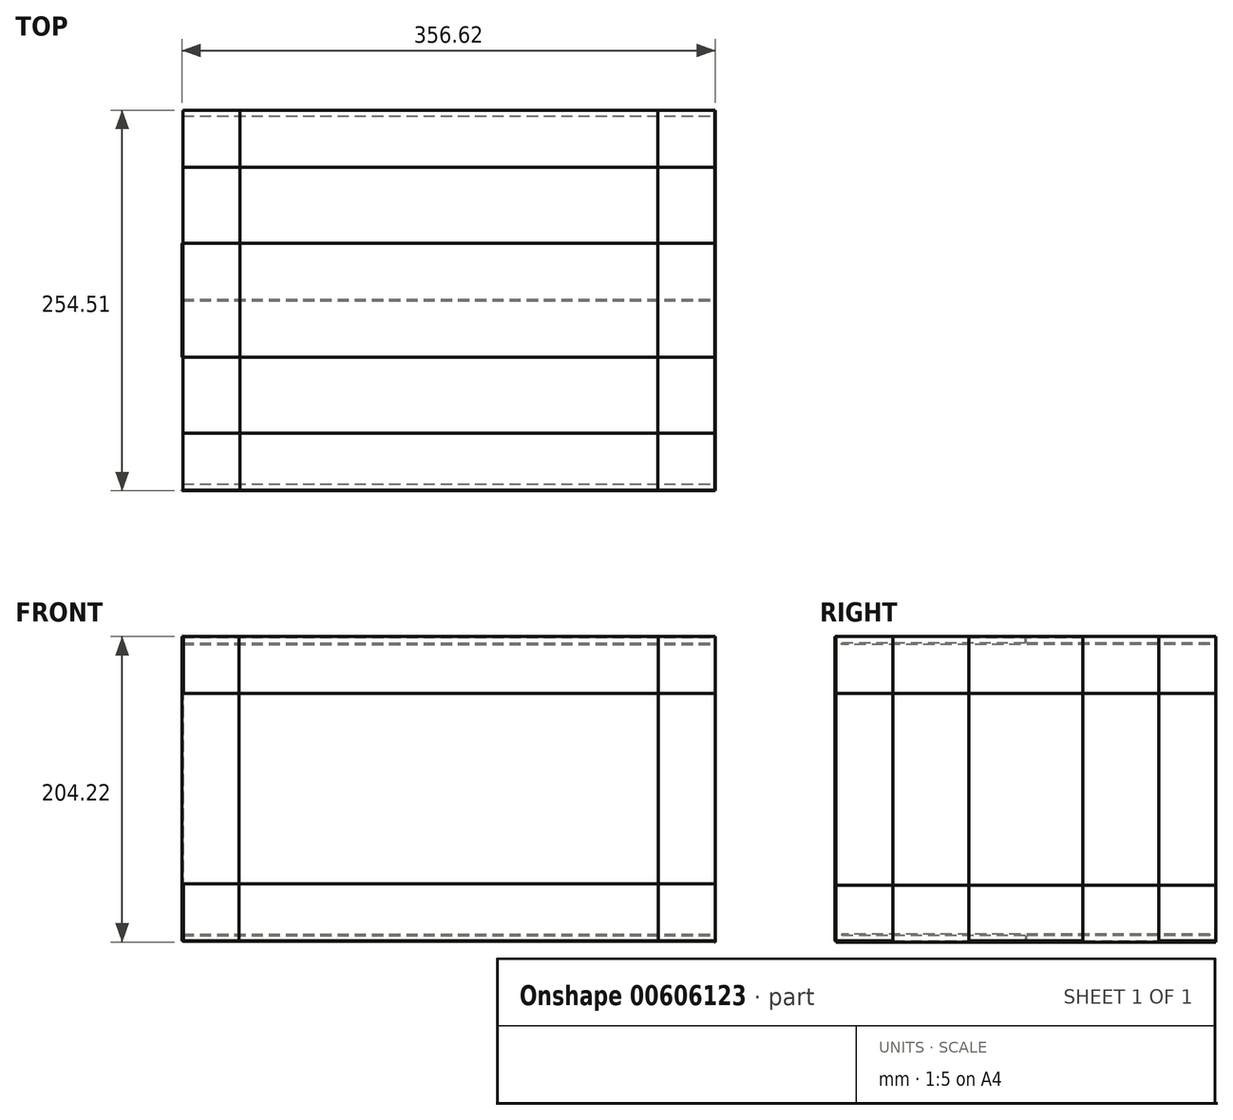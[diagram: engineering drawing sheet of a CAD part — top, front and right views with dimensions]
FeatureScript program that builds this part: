
annotation { "Feature Type Name" : "Feature", "Feature Type Description" : "" }
export const myFeature = defineFeature(function(context is Context, id is Id, definition is map)
    precondition{}
    {
        {
            var Q0;
            Q0=qCreatedBy(makeId("Top.planeOp"),FACE);
            var sketch = newSketch(context, id + "F0", { "sketchPlane" : qUnion([Q0])});
            skLineSegment(sketch, "E0.bottom", {"start": v(177.8, 127) * mm, "end": v(-177.8, 127) * mm});
            skLineSegment(sketch, "E0.top", {"start": v(177.8, -127) * mm, "end": v(-177.8, -127) * mm});
            skLineSegment(sketch, "E0.left", {"start": v(177.8, 127) * mm, "end": v(177.8, -127) * mm});
            skLineSegment(sketch, "E0.right", {"start": v(-177.8, 127) * mm, "end": v(-177.8, -127) * mm});
            skPoint(sketch, "E0.middle", {"position": v(0, 0) * mm});
            skSolve(sketch);
        }
        {
            var Q0;
            Q0=makeQuery(id+"F0.imprint","IMPRINT",FACE,{"disambiguationData":[TD([[makeQuery(id+"F0.imprint","IMPRINT",EDGE,{"derivedFrom":sQuery(id+"F0.wireOp",EDGE,"E0.bottom")}),1.0]])]});
            extrude(context, id + "F1", {"entities" : qUnion([Q0]), "depth" : 203.2 * mm, "offsetDistance" : 25.4 * mm});
        }
        {
            var Q0;
            Q0=makeQuery(id+"F1.opExtrude","CAP_FACE",FACE,{"disambiguationData":[OSD([sQuery(id+"F0.wireOp",EDGE,"E0.bottom"),sQuery(id+"F0.wireOp",EDGE,"E0.top"),sQuery(id+"F0.wireOp",EDGE,"E0.left"),sQuery(id+"F0.wireOp",EDGE,"E0.right")])],"isStart":false});
            var sketch = newSketch(context, id + "F2", { "sketchPlane" : qUnion([Q0])});
            skLineSegment(sketch, "E1.0", {"start": v(-177.8, -0.4) * mm, "end": v(177.8, -0.4) * mm});
            skLineSegment(sketch, "E2.0", {"start": v(-177.8, 0.4) * mm, "end": v(177.8, 0.4) * mm});
            skSolve(sketch);
        }
        {
            var Q0;
            {var subQ0=sQuery(id+"F2.wireOp",EDGE,"E1.0");Q0=makeQuery(id+"F2.imprint","IMPRINT",FACE,{"disambiguationData":[TD([[makeQuery(id+"F2.imprint","IMPRINT",EDGE,{"derivedFrom":subQ0}),1.0]])]});}
            extrude(context, id + "F3", {"entities" : qUnion([Q0]), "operationType" : NewBodyOperationType.REMOVE, "oppositeDirection" : true, "depth" : 3.96 * mm, "offsetDistance" : 25.4 * mm});
        }
        {
            var Q0;
            Q0=makeQuery(id+"F1.opExtrude","CAP_FACE",FACE,{"disambiguationData":[OSD([sQuery(id+"F0.wireOp",EDGE,"E0.bottom"),sQuery(id+"F0.wireOp",EDGE,"E0.top"),sQuery(id+"F0.wireOp",EDGE,"E0.left"),sQuery(id+"F0.wireOp",EDGE,"E0.right")])],"isStart":true});
            var sketch = newSketch(context, id + "F4", { "sketchPlane" : qUnion([Q0])});
            skLineSegment(sketch, "E3.0", {"start": v(-177.8, -0.4) * mm, "end": v(177.8, -0.4) * mm});
            skLineSegment(sketch, "E4.0", {"start": v(-177.8, 0.4) * mm, "end": v(177.8, 0.4) * mm});
            skPoint(sketch, "E5.end.orphan", {"position": v(177.8, 0) * mm});
            skPoint(sketch, "E5.start.orphan", {"position": v(-177.8, 0) * mm});
            skSolve(sketch);
        }
        {
            var Q0;
            Q0=qSketchRegion(id+"F4",true);
            var Q1;
            {var subQ0=sQuery(id+"F4.wireOp",EDGE,"E3.0");Q1=makeQuery(id+"F4.imprint","IMPRINT",FACE,{"disambiguationData":[TD([[makeQuery(id+"F4.imprint","IMPRINT",EDGE,{"derivedFrom":subQ0}),1.0]])]});}
            extrude(context, id + "F5", {"entities" : qUnion([Q0, Q1]), "operationType" : NewBodyOperationType.REMOVE, "oppositeDirection" : true, "depth" : 3.96 * mm, "offsetDistance" : 25.4 * mm});
        }
        {
            var Q0;
            {var subQ0=sQuery(id+"F0.wireOp",EDGE,"E0.top");var subQ1=sQuery(id+"F0.wireOp",EDGE,"E0.left");var subQ2=sQuery(id+"F0.wireOp",EDGE,"E0.right");Q0=makeQuery(id+"F3.boolean.opBoolean","SPLIT",FACE,{"disambiguationData":[TD([makeQuery(id+"F1.opExtrude","SWEPT_FACE",FACE,{"disambiguationData":[OSD([subQ0])]})])],"derivedFrom":makeQuery(id+"F1.opExtrude","CAP_FACE",FACE,{"disambiguationData":[OSD([sQuery(id+"F0.wireOp",EDGE,"E0.bottom"),subQ0,subQ1,subQ2])],"isStart":false})});}
            var sketch = newSketch(context, id + "F6", { "sketchPlane" : qUnion([Q0])});
            skLineSegment(sketch, "E6.bottom", {"start": v(177.8, -38.1) * mm, "end": v(-177.8, -38.1) * mm});
            skLineSegment(sketch, "E6.top", {"start": v(177.8, 38.1) * mm, "end": v(-177.8, 38.1) * mm});
            skLineSegment(sketch, "E6.left", {"start": v(177.8, -38.1) * mm, "end": v(177.8, 38.1) * mm});
            skLineSegment(sketch, "E6.right", {"start": v(-177.8, -38.1) * mm, "end": v(-177.8, 38.1) * mm});
            skPoint(sketch, "E6.middle", {"position": v(0, 0) * mm});
            skLineSegment(sketch, "E7.top", {"start": v(-177.8, 38.1) * mm, "end": v(-139.7, 38.1) * mm});
            skLineSegment(sketch, "E8.bottom", {"start": v(-177.8, -38.1) * mm, "end": v(-139.7, -38.1) * mm});
            skLineSegment(sketch, "E9.top", {"start": v(177.8, 38.1) * mm, "end": v(139.7, 38.1) * mm});
            skLineSegment(sketch, "E10.bottom", {"start": v(177.8, -38.1) * mm, "end": v(139.7, -38.1) * mm});
            skSolve(sketch);
        }
        {
            var Q0;
            Q0=qSketchRegion(id+"F6",true);
            extrude(context, id + "F7", {"entities" : qUnion([Q0]), "depth" : 0.5 * mm, "offsetDistance" : 25.4 * mm});
        }
        {
            var Q0;
            Q0=makeQuery(id+"F7.opExtrude","SWEPT_FACE",FACE,{"disambiguationData":[OSD([sQuery(id+"F6.wireOp",EDGE,"E6.left")])]});
            var sketch = newSketch(context, id + "F8", { "sketchPlane" : qUnion([Q0])});
            skLineSegment(sketch, "E11.bottom", {"start": v(-38.1, 203.7) * mm, "end": v(38.1, 203.7) * mm});
            skLineSegment(sketch, "E11.top", {"start": v(-38.1, 0.46) * mm, "end": v(38.1, 0.46) * mm});
            skLineSegment(sketch, "E11.left", {"start": v(-38.1, 203.7) * mm, "end": v(-38.1, 0.46) * mm});
            skLineSegment(sketch, "E11.right", {"start": v(38.1, 203.7) * mm, "end": v(38.1, 0.46) * mm});
            skSolve(sketch);
        }
        {
            var Q0;
            Q0=qSketchRegion(id+"F8",true);
            extrude(context, id + "F9", {"entities" : qUnion([Q0]), "depth" : 0.5 * mm, "offsetDistance" : 25.4 * mm});
        }
        {
            var Q0;
            Q0=makeQuery(id+"F1.opExtrude","SWEPT_FACE",FACE,{"disambiguationData":[OSD([sQuery(id+"F0.wireOp",EDGE,"E0.left")])]});
            var sketch = newSketch(context, id + "F10", { "sketchPlane" : qUnion([Q0])});
            skLineSegment(sketch, "E12.bottom", {"start": v(123.04, 198.44) * mm, "end": v(-123.04, 198.44) * mm});
            skLineSegment(sketch, "E12.top", {"start": v(123.04, 199.24) * mm, "end": v(-123.04, 199.24) * mm});
            skLineSegment(sketch, "E12.left", {"start": v(123.04, 198.44) * mm, "end": v(123.04, 199.24) * mm});
            skLineSegment(sketch, "E12.right", {"start": v(-123.04, 198.44) * mm, "end": v(-123.04, 199.24) * mm});
            skPoint(sketch, "E12.middle", {"position": v(0, 198.84) * mm});
            skPoint(sketch, "E12.middle.positionSnap0", {"position": v(0, 199.24) * mm});
            skPoint(sketch, "E12.centerSnap0", {"position": v(0, 199.24) * mm});
            skLineSegment(sketch, "E13", {"start": v(-127, 101.6) * mm, "end": v(-92.27, 101.6) * mm, "construction": true});
            skLineSegment(sketch, "E14.MirrorCS", {"start": v(123.04, 4.76) * mm, "end": v(123.04, 3.96) * mm});
            skPoint(sketch, "E15.MirrorP", {"position": v(0, 4.36) * mm});
            skLineSegment(sketch, "E16.MirrorCS", {"start": v(-123.04, 4.76) * mm, "end": v(-123.04, 3.96) * mm});
            skPoint(sketch, "E17.MirrorP", {"position": v(0, 3.96) * mm});
            skLineSegment(sketch, "E18.MirrorCS", {"start": v(123.04, 4.76) * mm, "end": v(-123.04, 4.76) * mm});
            skLineSegment(sketch, "E19.MirrorCS", {"start": v(123.04, 3.96) * mm, "end": v(-123.04, 3.96) * mm});
            skSolve(sketch);
        }
        {
            var Q0;
            Q0=qSketchRegion(id+"F10",true);
            extrude(context, id + "F11", {"entities" : qUnion([Q0]), "operationType" : NewBodyOperationType.REMOVE, "endBound" : BoundingType.THROUGH_ALL, "oppositeDirection" : true, "depth" : 25.4 * mm, "offsetDistance" : 25.4 * mm});
        }
        {
            var Q0;
            {var subQ0=sQuery(id+"F0.wireOp",EDGE,"E0.top");var subQ1=sQuery(id+"F0.wireOp",EDGE,"E0.left");var subQ2=sQuery(id+"F0.wireOp",EDGE,"E0.right");Q0=makeQuery(id+"F3.boolean.opBoolean","SPLIT",FACE,{"disambiguationData":[TD([makeQuery(id+"F1.opExtrude","SWEPT_FACE",FACE,{"disambiguationData":[OSD([subQ0])]})])],"derivedFrom":makeQuery(id+"F1.opExtrude","CAP_FACE",FACE,{"disambiguationData":[OSD([sQuery(id+"F0.wireOp",EDGE,"E0.bottom"),subQ0,subQ1,subQ2])],"isStart":false})});}
            var sketch = newSketch(context, id + "F12", { "sketchPlane" : qUnion([Q0])});
            skLineSegment(sketch, "E20.bottom", {"start": v(-177.8, -127) * mm, "end": v(177.8, -127) * mm});
            skLineSegment(sketch, "E20.top", {"start": v(-177.8, -88.9) * mm, "end": v(177.8, -88.9) * mm});
            skLineSegment(sketch, "E20.left", {"start": v(-177.8, -127) * mm, "end": v(-177.8, -88.9) * mm});
            skLineSegment(sketch, "E20.right", {"start": v(177.8, -127) * mm, "end": v(177.8, -88.9) * mm});
            skLineSegment(sketch, "E21.bottom", {"start": v(-177.8, 127) * mm, "end": v(177.8, 127) * mm});
            skLineSegment(sketch, "E21.top", {"start": v(-177.8, 88.9) * mm, "end": v(177.8, 88.9) * mm});
            skLineSegment(sketch, "E21.left", {"start": v(-177.8, 127) * mm, "end": v(-177.8, 88.9) * mm});
            skLineSegment(sketch, "E21.right", {"start": v(177.8, 127) * mm, "end": v(177.8, 88.9) * mm});
            skSolve(sketch);
        }
        {
            var Q0;
            Q0 = qSketchRegion(id + "F12", true);
            extrude(context, id + "F13", {"entities" : qUnion([Q0]), "depth" : 0.5 * mm, "offsetDistance" : 25.4 * mm});
        }
        {
            var Q0;
            {var subQ0=sQuery(id+"F0.wireOp",EDGE,"E0.bottom");var subQ1=sQuery(id+"F0.wireOp",EDGE,"E0.right");var subQ2=sQuery(id+"F0.wireOp",EDGE,"E0.left");Q0=makeQuery(id+"F3.boolean.opBoolean","SPLIT",FACE,{"disambiguationData":[TD([makeQuery(id+"F1.opExtrude","SWEPT_FACE",FACE,{"disambiguationData":[OSD([subQ0])]})])],"derivedFrom":makeQuery(id+"F1.opExtrude","CAP_FACE",FACE,{"disambiguationData":[OSD([subQ0,sQuery(id+"F0.wireOp",EDGE,"E0.top"),subQ2,subQ1])],"isStart":false})});}
            var sketch = newSketch(context, id + "F14", { "sketchPlane" : qUnion([Q0])});
            skLineSegment(sketch, "E22.bottom", {"start": v(-177.8, 127) * mm, "end": v(-139.7, 127) * mm});
            skLineSegment(sketch, "E22.top", {"start": v(-177.8, -127) * mm, "end": v(-139.7, -127) * mm});
            skLineSegment(sketch, "E22.left", {"start": v(-177.8, 127) * mm, "end": v(-177.8, -127) * mm});
            skLineSegment(sketch, "E22.right", {"start": v(-139.7, 127) * mm, "end": v(-139.7, -127) * mm});
            skLineSegment(sketch, "E23.bottom", {"start": v(177.8, 127) * mm, "end": v(139.7, 127) * mm});
            skLineSegment(sketch, "E23.top", {"start": v(177.8, -127) * mm, "end": v(139.7, -127) * mm});
            skLineSegment(sketch, "E23.left", {"start": v(177.8, 127) * mm, "end": v(177.8, -127) * mm});
            skLineSegment(sketch, "E23.right", {"start": v(139.7, 127) * mm, "end": v(139.7, -127) * mm});
            skSolve(sketch);
        }
        {
            var Q0;
            Q0 = qSketchRegion(id + "F14", true);
            extrude(context, id + "F15", {"entities" : qUnion([Q0]), "depth" : 0.5 * mm, "offsetDistance" : 25.4 * mm});
        }
        {
            var Q0;
            Q0=makeQuery(id+"F9.opExtrude","SWEPT_BODY",BODY,{"disambiguationData":[OSD([sQuery(id+"F8.wireOp",EDGE,"E11.bottom"),sQuery(id+"F8.wireOp",EDGE,"E11.top"),sQuery(id+"F8.wireOp",EDGE,"E11.left"),sQuery(id+"F8.wireOp",EDGE,"E11.right")])]});
            var Q1;
            Q1=qCreatedBy(makeId("Right.planeOp"),FACE);
            mirror(context, id + "F16", {"entities" : qUnion([Q0]), "mirrorPlane" : qUnion([Q1])});
        }
        {
            var Q0;
            Q0=makeQuery(id+"F15.opExtrude","SWEPT_FACE",FACE,{"disambiguationData":[OSD([sQuery(id+"F14.wireOp",EDGE,"E23.left")])]});
            var sketch = newSketch(context, id + "F17", { "sketchPlane" : qUnion([Q0])});
            skLineSegment(sketch, "E24.bottom", {"start": v(-127, 203.7) * mm, "end": v(-88.9, 203.7) * mm});
            skLineSegment(sketch, "E24.top", {"start": v(-127, 0.4) * mm, "end": v(-88.9, 0.4) * mm});
            skLineSegment(sketch, "E24.left", {"start": v(-127, 203.7) * mm, "end": v(-127, 0.4) * mm});
            skLineSegment(sketch, "E24.right", {"start": v(-88.9, 203.7) * mm, "end": v(-88.9, 0.4) * mm});
            skLineSegment(sketch, "E25", {"start": v(0, 0) * mm, "end": v(0, 11.94) * mm, "construction": true});
            skLineSegment(sketch, "E26.MirrorCS", {"start": v(127, 0.4) * mm, "end": v(88.9, 0.4) * mm});
            skLineSegment(sketch, "E27.MirrorCS", {"start": v(127, 203.7) * mm, "end": v(88.9, 203.7) * mm});
            skLineSegment(sketch, "E28.MirrorCS", {"start": v(88.9, 203.7) * mm, "end": v(88.9, 0.4) * mm});
            skLineSegment(sketch, "E29.MirrorCS", {"start": v(127, 203.7) * mm, "end": v(127, 0.4) * mm});
            skSolve(sketch);
        }
        {
            var Q0;
            Q0 = qSketchRegion(id + "F17", true);
            extrude(context, id + "F18", {"entities" : qUnion([Q0]), "depth" : 0.5 * mm, "offsetDistance" : 25.4 * mm});
        }
        {
            var Q0;
            Q0=makeQuery(id+"F15.opExtrude","SWEPT_FACE",FACE,{"disambiguationData":[OSD([sQuery(id+"F14.wireOp",EDGE,"E23.left")])]});
            var sketch = newSketch(context, id + "F19", { "sketchPlane" : qUnion([Q0])});
            skLineSegment(sketch, "E30.bottom", {"start": v(-127, 203.7) * mm, "end": v(127, 203.7) * mm});
            skLineSegment(sketch, "E30.top", {"start": v(-127, 165.6) * mm, "end": v(127, 165.6) * mm});
            skLineSegment(sketch, "E30.left", {"start": v(-127, 203.7) * mm, "end": v(-127, 165.6) * mm});
            skLineSegment(sketch, "E30.right", {"start": v(127, 203.7) * mm, "end": v(127, 165.6) * mm});
            skLineSegment(sketch, "E31", {"start": v(-78.01, 0) * mm, "end": v(-63.77, 0) * mm});
            skLineSegment(sketch, "E32.0", {"start": v(-78.01, 101.6) * mm, "end": v(-63.77, 101.6) * mm, "construction": true});
            skLineSegment(sketch, "E33.MirrorCS", {"start": v(-127, 37.6) * mm, "end": v(127, 37.6) * mm});
            skLineSegment(sketch, "E34.MirrorCS", {"start": v(-127, -0.5) * mm, "end": v(-127, 37.6) * mm});
            skLineSegment(sketch, "E35.MirrorCS", {"start": v(127, -0.5) * mm, "end": v(127, 37.6) * mm});
            skLineSegment(sketch, "E36.MirrorCS", {"start": v(-127, -0.5) * mm, "end": v(127, -0.5) * mm});
            skSolve(sketch);
        }
        {
            var Q0;
            Q0 = qSketchRegion(id + "F19", true);
            extrude(context, id + "F20", {"entities" : qUnion([Q0]), "depth" : 0.5 * mm, "offsetDistance" : 25.4 * mm});
        }
        {
            var Q0;
            Q0=makeQuery(id+"F18.opExtrude","SWEPT_FACE",FACE,{"disambiguationData":[OSD([sQuery(id+"F17.wireOp",EDGE,"E24.left")])]});
            var sketch = newSketch(context, id + "F21", { "sketchPlane" : qUnion([Q0])});
            skLineSegment(sketch, "E37.bottom", {"start": v(178.3, 203.7) * mm, "end": v(-177.4, 203.7) * mm});
            skLineSegment(sketch, "E37.top", {"start": v(178.3, 165.6) * mm, "end": v(-177.4, 165.6) * mm});
            skLineSegment(sketch, "E37.left", {"start": v(178.3, 203.7) * mm, "end": v(178.3, 165.6) * mm});
            skLineSegment(sketch, "E37.right", {"start": v(-177.4, 203.7) * mm, "end": v(-177.4, 165.6) * mm});
            skLineSegment(sketch, "E38", {"start": v(178.3, 102.06) * mm, "end": v(91.63, 102.06) * mm, "construction": true});
            skPoint(sketch, "E38.endSnap0", {"position": v(178.3, 102.06) * mm});
            skLineSegment(sketch, "E39.MirrorCS", {"start": v(178.3, 38.5) * mm, "end": v(-177.4, 38.5) * mm});
            skLineSegment(sketch, "E40.MirrorCS", {"start": v(178.3, 0.4) * mm, "end": v(-177.4, 0.4) * mm});
            skLineSegment(sketch, "E41.MirrorCS", {"start": v(-177.4, 0.4) * mm, "end": v(-177.4, 38.5) * mm});
            skLineSegment(sketch, "E42.MirrorCS", {"start": v(178.3, 0.4) * mm, "end": v(178.3, 38.5) * mm});
            skSolve(sketch);
        }
        {
            var Q0;
            Q0 = qSketchRegion(id + "F21", true);
            extrude(context, id + "F22", {"entities" : qUnion([Q0]), "depth" : 0.5 * mm, "offsetDistance" : 25.4 * mm});
        }
        {
            var Q0;
            Q0=makeQuery(id+"F18.opExtrude","SWEPT_FACE",FACE,{"disambiguationData":[OSD([sQuery(id+"F17.wireOp",EDGE,"E24.left")])]});
            var sketch = newSketch(context, id + "F23", { "sketchPlane" : qUnion([Q0])});
            skLineSegment(sketch, "E43.bottom", {"start": v(178.3, 203.7) * mm, "end": v(140.2, 203.7) * mm});
            skLineSegment(sketch, "E43.top", {"start": v(178.3, 0.4) * mm, "end": v(140.2, 0.4) * mm});
            skLineSegment(sketch, "E43.left", {"start": v(178.3, 203.7) * mm, "end": v(178.3, 0.4) * mm});
            skLineSegment(sketch, "E43.right", {"start": v(140.2, 203.7) * mm, "end": v(140.2, 0.4) * mm});
            skLineSegment(sketch, "E44", {"start": v(0, 0) * mm, "end": v(0, 44.96) * mm, "construction": true});
            skLineSegment(sketch, "E45.MirrorCS", {"start": v(-140.2, 203.7) * mm, "end": v(-140.2, 0.4) * mm});
            skLineSegment(sketch, "E46.MirrorCS", {"start": v(-178.3, 203.7) * mm, "end": v(-178.3, 0.4) * mm});
            skLineSegment(sketch, "E47.MirrorCS", {"start": v(-178.3, 203.7) * mm, "end": v(-140.2, 203.7) * mm});
            skLineSegment(sketch, "E48.MirrorCS", {"start": v(-178.3, 0.4) * mm, "end": v(-140.2, 0.4) * mm});
            skSolve(sketch);
        }
        {
            var Q0;
            Q0 = qSketchRegion(id + "F23", true);
            extrude(context, id + "F24", {"entities" : qUnion([Q0]), "depth" : 0.5 * mm, "offsetDistance" : 25.4 * mm});
        }
    });
